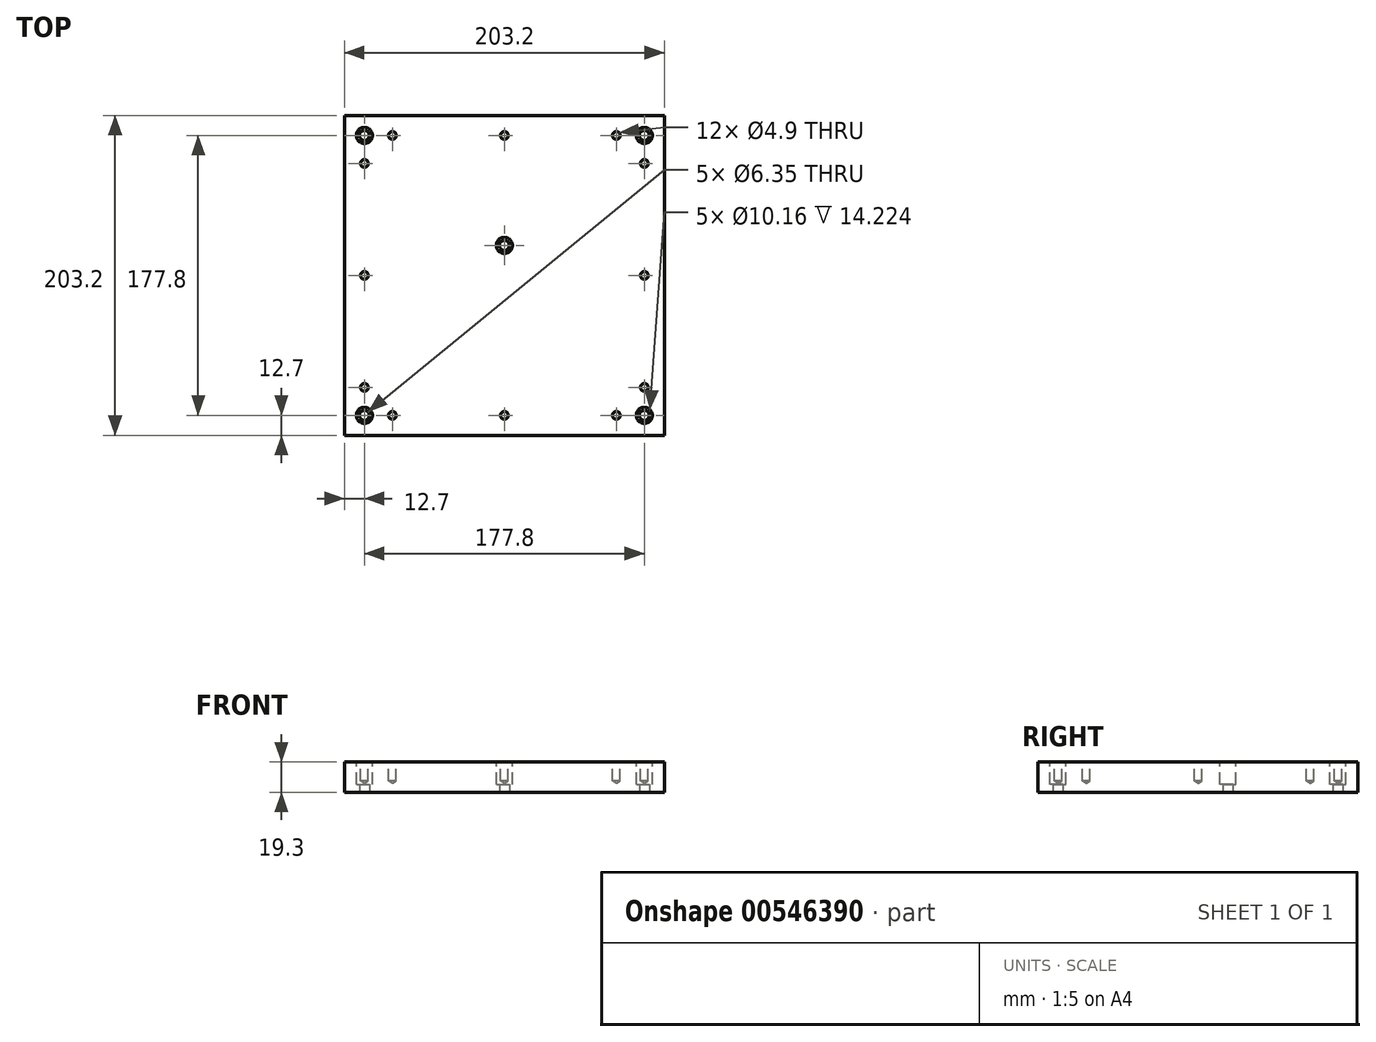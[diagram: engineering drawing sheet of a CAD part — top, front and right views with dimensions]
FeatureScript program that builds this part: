
annotation { "Feature Type Name" : "Feature", "Feature Type Description" : "" }
export const myFeature = defineFeature(function(context is Context, id is Id, definition is map)
    precondition{}
    {
        {
            var Q0;
            Q0=qCreatedBy(makeId("Top.planeOp"),FACE);
            var sketch = newSketch(context, id + "F0", { "sketchPlane" : qUnion([Q0])});
            skLineSegment(sketch, "E0.rect.bottom", {"start": v(101.6, -101.6) * mm, "end": v(-101.6, -101.6) * mm});
            skLineSegment(sketch, "E0.rect.top", {"start": v(101.6, 101.6) * mm, "end": v(-101.6, 101.6) * mm});
            skLineSegment(sketch, "E0.rect.left", {"start": v(101.6, -101.6) * mm, "end": v(101.6, 101.6) * mm});
            skLineSegment(sketch, "E0.rect.right", {"start": v(-101.6, -101.6) * mm, "end": v(-101.6, 101.6) * mm});
            skPoint(sketch, "E0.rect.middle", {"position": v(0, 0) * mm});
            skCircle(sketch, "E1", {"center": v(88.9, 88.9) * mm, "radius": 3.18 * mm});
            skCircle(sketch, "E2", {"center": v(-88.9, 88.9) * mm, "radius": 3.18 * mm});
            skCircle(sketch, "E3", {"center": v(-88.9, -88.9) * mm, "radius": 3.18 * mm});
            skCircle(sketch, "E4", {"center": v(88.9, -88.9) * mm, "radius": 3.18 * mm});
            skLineSegment(sketch, "E5.rect.bottom", {"start": v(88.9, 88.9) * mm, "end": v(-88.9, 88.9) * mm, "construction": true});
            skLineSegment(sketch, "E5.rect.top", {"start": v(88.9, -88.9) * mm, "end": v(-88.9, -88.9) * mm, "construction": true});
            skLineSegment(sketch, "E5.rect.left", {"start": v(88.9, 88.9) * mm, "end": v(88.9, -88.9) * mm, "construction": true});
            skLineSegment(sketch, "E5.rect.right", {"start": v(-88.9, 88.9) * mm, "end": v(-88.9, -88.9) * mm, "construction": true});
            skCircle(sketch, "E6", {"center": v(0, 19.05) * mm, "radius": 3.18 * mm});
            skPoint(sketch, "E7", {"position": v(-88.9, 0) * mm});
            skPoint(sketch, "E8", {"position": v(0, 88.9) * mm});
            skPoint(sketch, "E9", {"position": v(88.9, 0) * mm});
            skPoint(sketch, "E10", {"position": v(0, -88.9) * mm});
            skSolve(sketch);
        }
        {
            var Q0;
            Q0=qSketchRegion(id+"F0",true);
            extrude(context, id + "F1", {"entities" : qUnion([Q0]), "depth" : 19.3 * mm});
        }
        {
            var Q0;
            Q0=makeQuery(id+"F1.opExtrude","CAP_FACE",FACE,{"disambiguationData":[OSD([sQuery(id+"F0.wireOp",EDGE,"E0.rect.bottom"),sQuery(id+"F0.wireOp",EDGE,"E0.rect.top"),sQuery(id+"F0.wireOp",EDGE,"E0.rect.left"),sQuery(id+"F0.wireOp",EDGE,"E0.rect.right"),sQuery(id+"F0.wireOp",EDGE,"E1"),sQuery(id+"F0.wireOp",EDGE,"E2"),sQuery(id+"F0.wireOp",EDGE,"E3"),sQuery(id+"F0.wireOp",EDGE,"E4"),sQuery(id+"F0.wireOp",EDGE,"E6")])],"isStart":false});
            var sketch = newSketch(context, id + "F2", { "sketchPlane" : qUnion([Q0])});
            skCircle(sketch, "E11", {"center": v(-88.9, 88.9) * mm, "radius": 5.08 * mm});
            skCircle(sketch, "E12", {"center": v(0, 19.05) * mm, "radius": 5.08 * mm});
            skCircle(sketch, "E13", {"center": v(88.9, 88.9) * mm, "radius": 5.08 * mm});
            skCircle(sketch, "E14", {"center": v(-88.9, -88.9) * mm, "radius": 5.08 * mm});
            skCircle(sketch, "E15", {"center": v(88.9, -88.9) * mm, "radius": 5.08 * mm});
            skPoint(sketch, "E16.0", {"position": v(0, 88.9) * mm});
            skPoint(sketch, "E16.1", {"position": v(0, -88.9) * mm});
            skPoint(sketch, "E16.2", {"position": v(88.9, 0) * mm});
            skPoint(sketch, "E16.3", {"position": v(-88.9, 0) * mm});
            skLineSegment(sketch, "E17.0", {"start": v(-88.9, 88.9) * mm, "end": v(-88.9, -88.9) * mm, "construction": true});
            skLineSegment(sketch, "E17.1", {"start": v(88.9, 88.9) * mm, "end": v(-88.9, 88.9) * mm, "construction": true});
            skLineSegment(sketch, "E17.2", {"start": v(88.9, 88.9) * mm, "end": v(88.9, -88.9) * mm, "construction": true});
            skLineSegment(sketch, "E17.3", {"start": v(88.9, -88.9) * mm, "end": v(-88.9, -88.9) * mm, "construction": true});
            skLineSegment(sketch, "E18", {"start": v(-88.9, 0) * mm, "end": v(88.9, 0) * mm, "construction": true});
            skLineSegment(sketch, "E19", {"start": v(0, 88.9) * mm, "end": v(0, -88.9) * mm, "construction": true});
            skPoint(sketch, "E20", {"position": v(-88.9, 71.12) * mm});
            skPoint(sketch, "E21", {"position": v(-71.12, 88.9) * mm});
            skPoint(sketch, "E22.MirrorP", {"position": v(71.12, 88.9) * mm});
            skPoint(sketch, "E23.MirrorP", {"position": v(88.9, 71.12) * mm});
            skPoint(sketch, "E24.MirrorP", {"position": v(88.9, -71.12) * mm});
            skPoint(sketch, "E25.MirrorP", {"position": v(71.12, -88.9) * mm});
            skPoint(sketch, "E26.MirrorP", {"position": v(-71.12, -88.9) * mm});
            skPoint(sketch, "E27.MirrorP", {"position": v(-88.9, -71.12) * mm});
            skSolve(sketch);
        }
        {
            var Q0;
            Q0=makeQuery(id+"F1.opExtrude","CAP_FACE",FACE,{"disambiguationData":[OSD([sQuery(id+"F0.wireOp",EDGE,"E0.rect.bottom"),sQuery(id+"F0.wireOp",EDGE,"E0.rect.top"),sQuery(id+"F0.wireOp",EDGE,"E0.rect.left"),sQuery(id+"F0.wireOp",EDGE,"E0.rect.right"),sQuery(id+"F0.wireOp",EDGE,"E1"),sQuery(id+"F0.wireOp",EDGE,"E2"),sQuery(id+"F0.wireOp",EDGE,"E3"),sQuery(id+"F0.wireOp",EDGE,"E4"),sQuery(id+"F0.wireOp",EDGE,"E6")])],"isStart":true});
            cPlane(context, id + "F3", {"entities" : qUnion([Q0]), "cplaneType" : CPlaneType.OFFSET, "offset" : 5.08 * mm, "oppositeDirection" : true, "width" : 152.4 * mm, "height" : 152.4 * mm});
        }
        {
            var Q0;
            Q0=qSketchRegion(id+"F2",true);
            var Q1;
            Q1=qCreatedBy(id+"F3.planeOp",FACE);
            extrude(context, id + "F4", {"entities" : qUnion([Q0]), "operationType" : NewBodyOperationType.REMOVE, "endBound" : BoundingType.UP_TO_SURFACE, "oppositeDirection" : true, "endBoundEntityFace" : qUnion([Q1]), "depth" : 25.4 * mm});
        }
        {
            var Q0;
            Q0=sQuery(id+"F2.wireOp",VERTEX,"E16.1");
            var Q1;
            Q1=sQuery(id+"F2.wireOp",VERTEX,"E16.2");
            var Q2;
            Q2=sQuery(id+"F2.wireOp",VERTEX,"E16.0");
            var Q3;
            Q3=sQuery(id+"F2.wireOp",VERTEX,"E16.3");
            var Q4;
            Q4=sQuery(id+"F2.wireOp",VERTEX,"E27.MirrorP");
            var Q5;
            Q5=sQuery(id+"F2.wireOp",VERTEX,"E26.MirrorP");
            var Q6;
            Q6=sQuery(id+"F2.wireOp",VERTEX,"E20");
            var Q7;
            Q7=sQuery(id+"F2.wireOp",VERTEX,"E21");
            var Q8;
            Q8=sQuery(id+"F2.wireOp",VERTEX,"E22.MirrorP");
            var Q9;
            Q9=sQuery(id+"F2.wireOp",VERTEX,"E23.MirrorP");
            var Q10;
            Q10=sQuery(id+"F2.wireOp",VERTEX,"E24.MirrorP");
            var Q11;
            Q11=sQuery(id+"F2.wireOp",VERTEX,"E25.MirrorP");
            var Q12;
            Q12=makeQuery(id+"F1.opExtrude","SWEPT_BODY",BODY,{"disambiguationData":[OSD([sQuery(id+"F0.wireOp",EDGE,"E0.rect.bottom"),sQuery(id+"F0.wireOp",EDGE,"E0.rect.top"),sQuery(id+"F0.wireOp",EDGE,"E0.rect.left"),sQuery(id+"F0.wireOp",EDGE,"E0.rect.right"),sQuery(id+"F0.wireOp",EDGE,"E1"),sQuery(id+"F0.wireOp",EDGE,"E2"),sQuery(id+"F0.wireOp",EDGE,"E3"),sQuery(id+"F0.wireOp",EDGE,"E4"),sQuery(id+"F0.wireOp",EDGE,"E6")])]});
            hole(context, id + "F5", {"style" : HoleStyle.SIMPLE, "endStyle" : HoleEndStyle.BLIND, "holeDiameter" : 4.9 * mm, "holeDepth" : 12 * mm, "isTappedThrough" : true, "tappedDepth" : 12.7 * mm, "tapClearance" : 3, "locations" : qUnion([Q0, Q1, Q2, Q3, Q4, Q5, Q6, Q7, Q8, Q9, Q10, Q11]), "scope" : qUnion([Q12])});
        }
    });
